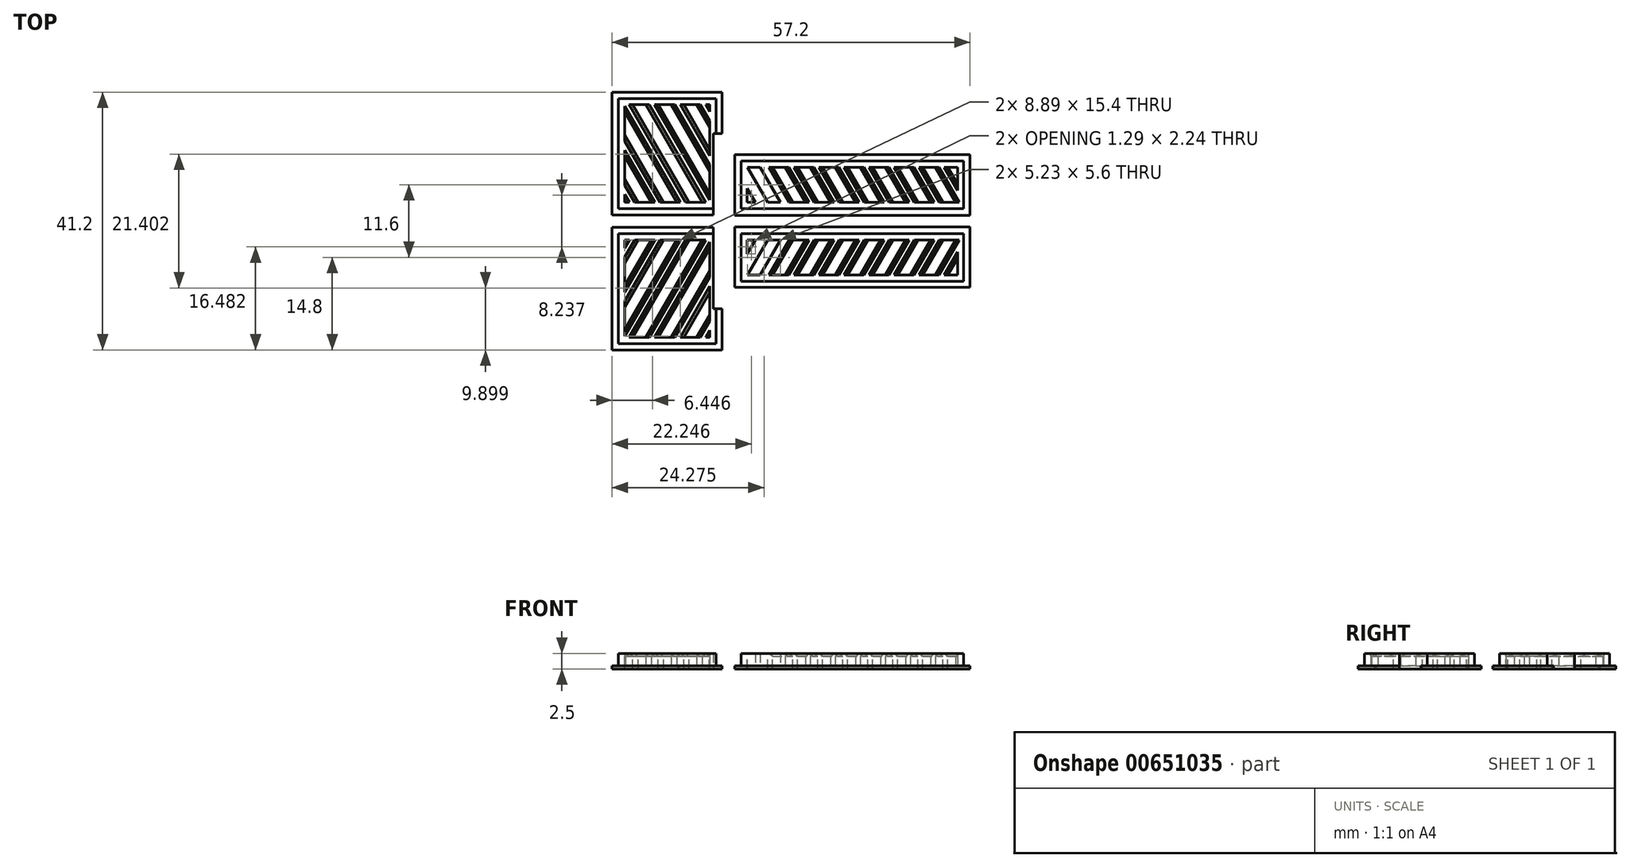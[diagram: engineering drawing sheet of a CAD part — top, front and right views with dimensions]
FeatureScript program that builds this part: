
annotation { "Feature Type Name" : "Feature", "Feature Type Description" : "" }
export const myFeature = defineFeature(function(context is Context, id is Id, definition is map)
    precondition{}
    {
        {
            var Q0;
            Q0=qCreatedBy(makeId("Top.planeOp"),FACE);
            var sketch = newSketch(context, id + "F0", { "sketchPlane" : qUnion([Q0])});
            skLineSegment(sketch, "E0.bottom", {"start": v(-17.6, 0) * mm, "end": v(-2, 0) * mm});
            skLineSegment(sketch, "E0.top", {"start": v(-17.6, 17.6) * mm, "end": v(-2, 17.6) * mm});
            skLineSegment(sketch, "E0.left", {"start": v(-17.6, 0) * mm, "end": v(-17.6, 17.6) * mm});
            skLineSegment(sketch, "E0.right", {"start": v(-2, 0) * mm, "end": v(-2, 17.6) * mm});
            skSolve(sketch);
        }
        {
            var Q0;
            Q0 = qSketchRegion(id + "F0", true);
            extrude(context, id + "F1", {"entities" : qUnion([Q0]), "depth" : 2.5 * mm, "offsetDistance" : 25 * mm});
        }
        {
            var Q0;
            Q0=qCreatedBy(makeId("Top.planeOp"),FACE);
            var sketch = newSketch(context, id + "F2", { "sketchPlane" : qUnion([Q0])});
            skLineSegment(sketch, "E1", {"start": v(-15.85, 0) * mm, "end": v(-26.01, 17.6) * mm});
            skLineSegment(sketch, "E2", {"start": v(-26.01, 17.6) * mm, "end": v(-24.01, 17.6) * mm});
            skLineSegment(sketch, "E3", {"start": v(-24.01, 17.6) * mm, "end": v(-13.85, 0) * mm});
            skLineSegment(sketch, "E4", {"start": v(-13.85, 0) * mm, "end": v(-15.85, 0) * mm});
            skLineSegment(sketch, "E5.1.0.0", {"start": v(-19.94, 17.6) * mm, "end": v(-9.78, 0) * mm});
            skLineSegment(sketch, "E5.1.0.1", {"start": v(-11.78, 0) * mm, "end": v(-21.94, 17.6) * mm});
            skLineSegment(sketch, "E5.1.0.2", {"start": v(-9.78, 0) * mm, "end": v(-11.78, 0) * mm});
            skLineSegment(sketch, "E5.1.0.3", {"start": v(-21.94, 17.6) * mm, "end": v(-19.94, 17.6) * mm});
            skLineSegment(sketch, "E5.2.0.0", {"start": v(-15.87, 17.6) * mm, "end": v(-5.7, 0) * mm});
            skLineSegment(sketch, "E5.2.0.1", {"start": v(-7.7, 0) * mm, "end": v(-17.87, 17.6) * mm});
            skLineSegment(sketch, "E5.2.0.2", {"start": v(-5.7, 0) * mm, "end": v(-7.7, 0) * mm});
            skLineSegment(sketch, "E5.2.0.3", {"start": v(-17.87, 17.6) * mm, "end": v(-15.87, 17.6) * mm});
            skLineSegment(sketch, "E5.3.0.0", {"start": v(-11.8, 17.6) * mm, "end": v(-1.64, 0) * mm});
            skLineSegment(sketch, "E5.3.0.1", {"start": v(-3.64, 0) * mm, "end": v(-13.8, 17.6) * mm});
            skLineSegment(sketch, "E5.3.0.2", {"start": v(-1.64, 0) * mm, "end": v(-3.64, 0) * mm});
            skLineSegment(sketch, "E5.3.0.3", {"start": v(-13.8, 17.6) * mm, "end": v(-11.8, 17.6) * mm});
            skLineSegment(sketch, "E5.4.0.0", {"start": v(-7.73, 17.6) * mm, "end": v(2.43, 0) * mm});
            skLineSegment(sketch, "E5.4.0.1", {"start": v(0.43, 0) * mm, "end": v(-9.73, 17.6) * mm});
            skLineSegment(sketch, "E5.4.0.2", {"start": v(2.43, 0) * mm, "end": v(0.43, 0) * mm});
            skLineSegment(sketch, "E5.4.0.3", {"start": v(-9.73, 17.6) * mm, "end": v(-7.73, 17.6) * mm});
            skLineSegment(sketch, "E5.direction1", {"start": v(-15.85, 0) * mm, "end": v(-11.78, 0) * mm, "construction": true});
            skLineSegment(sketch, "E6.0.5.0", {"start": v(-3.66, 17.6) * mm, "end": v(6.5, 0) * mm});
            skLineSegment(sketch, "E6.3.5.0", {"start": v(4.5, 0) * mm, "end": v(-5.66, 17.6) * mm});
            skLineSegment(sketch, "E6.6.5.0", {"start": v(6.5, 0) * mm, "end": v(4.5, 0) * mm});
            skLineSegment(sketch, "E6.9.5.0", {"start": v(-5.66, 17.6) * mm, "end": v(-3.66, 17.6) * mm});
            skLineSegment(sketch, "E7.bottom", {"start": v(-27.74, 19.26) * mm, "end": v(8.02, 19.26) * mm});
            skLineSegment(sketch, "E7.top", {"start": v(-27.74, -2) * mm, "end": v(8.02, -2) * mm});
            skLineSegment(sketch, "E7.left", {"start": v(-27.74, 19.26) * mm, "end": v(-27.74, -2) * mm});
            skLineSegment(sketch, "E7.right", {"start": v(8.02, 19.26) * mm, "end": v(8.02, -2) * mm});
            skSolve(sketch);
        }
        {
            var Q0;
            Q0 = qSketchRegion(id + "F2", true);
            extrude(context, id + "F3", {"entities" : qUnion([Q0]), "operationType" : NewBodyOperationType.REMOVE, "depth" : 10 * mm, "offsetDistance" : 25 * mm});
        }
        {
            var Q0;
            Q0=qCreatedBy(makeId("Top.planeOp"),FACE);
            var sketch = newSketch(context, id + "F4", { "sketchPlane" : qUnion([Q0])});
            skLineSegment(sketch, "E8.bottom", {"start": v(-17.6, 17.6) * mm, "end": v(-2, 17.6) * mm});
            skLineSegment(sketch, "E8.top", {"start": v(-17.6, 0) * mm, "end": v(-2, 0) * mm});
            skLineSegment(sketch, "E8.left", {"start": v(-17.6, 17.6) * mm, "end": v(-17.6, 0) * mm});
            skLineSegment(sketch, "E8.right", {"start": v(-2, 17.6) * mm, "end": v(-2, 0) * mm});
            skLineSegment(sketch, "E9.bottom", {"start": v(-16.6, 16.6) * mm, "end": v(-3, 16.6) * mm});
            skLineSegment(sketch, "E9.top", {"start": v(-16.6, 1) * mm, "end": v(-3, 1) * mm});
            skLineSegment(sketch, "E9.left", {"start": v(-16.6, 16.6) * mm, "end": v(-16.6, 1) * mm});
            skLineSegment(sketch, "E9.right", {"start": v(-3, 16.6) * mm, "end": v(-3, 1) * mm});
            skSolve(sketch);
        }
        {
            var Q0;
            Q0 = qSketchRegion(id + "F4", true);
            extrude(context, id + "F5", {"entities" : qUnion([Q0]), "operationType" : NewBodyOperationType.ADD, "depth" : 2.5 * mm, "offsetDistance" : 25 * mm});
        }
        {
            var Q0;
            {var subQ0=sQuery(id+"F0.wireOp",EDGE,"E0.top");var subQ2=sQuery(id+"F0.wireOp",EDGE,"E0.right");var subQ4=sQuery(id+"F0.wireOp",EDGE,"E0.bottom");var subQ6=sQuery(id+"F0.wireOp",EDGE,"E0.left");var subQ7=makeQuery(id+"F1.opExtrude","CAP_FACE",FACE,{"disambiguationData":[OSD([subQ4,subQ0,subQ6,subQ2])],"isStart":true});Q0=makeQuery(id+"F5.boolean.opBoolean","MERGE",FACE,{"derivedFrom":[makeQuery(id+"F3.boolean.opBoolean","SPLIT",FACE,{"disambiguationData":[TD([makeQuery(id+"F3.opExtrude","SWEPT_FACE",FACE,{"disambiguationData":[OSD([sQuery(id+"F2.wireOp",EDGE,"E1")])]})])],"derivedFrom":subQ7}),makeQuery(id+"F3.boolean.opBoolean","SPLIT",FACE,{"disambiguationData":[TD([makeQuery(id+"F3.opExtrude","SWEPT_FACE",FACE,{"disambiguationData":[OSD([sQuery(id+"F2.wireOp",EDGE,"E5.1.0.0")])]})])],"derivedFrom":subQ7}),makeQuery(id+"F3.boolean.opBoolean","SPLIT",FACE,{"disambiguationData":[TD([makeQuery(id+"F3.opExtrude","SWEPT_FACE",FACE,{"disambiguationData":[OSD([sQuery(id+"F2.wireOp",EDGE,"E5.4.0.0")])]})])],"derivedFrom":subQ7}),makeQuery(id+"F3.boolean.opBoolean","SPLIT",FACE,{"disambiguationData":[TD([makeQuery(id+"F3.opExtrude","SWEPT_FACE",FACE,{"disambiguationData":[OSD([sQuery(id+"F2.wireOp",EDGE,"E6.0.5.0")])]})])],"derivedFrom":subQ7}),makeQuery(id+"F3.boolean.opBoolean","SPLIT",FACE,{"disambiguationData":[TD([makeQuery(id+"F3.opExtrude","SWEPT_FACE",FACE,{"disambiguationData":[OSD([sQuery(id+"F2.wireOp",EDGE,"E5.2.0.0")])]})])],"derivedFrom":subQ7}),makeQuery(id+"F3.boolean.opBoolean","SPLIT",FACE,{"disambiguationData":[TD([makeQuery(id+"F3.opExtrude","SWEPT_FACE",FACE,{"disambiguationData":[OSD([sQuery(id+"F2.wireOp",EDGE,"E5.3.0.0")])]})])],"derivedFrom":subQ7}),makeQuery(id+"F5.opExtrude","CAP_FACE",FACE,{"disambiguationData":[OSD([sQuery(id+"F4.wireOp",EDGE,"E8.bottom"),sQuery(id+"F4.wireOp",EDGE,"E8.top"),sQuery(id+"F4.wireOp",EDGE,"E8.left"),sQuery(id+"F4.wireOp",EDGE,"E8.right"),sQuery(id+"F4.wireOp",EDGE,"E9.bottom"),sQuery(id+"F4.wireOp",EDGE,"E9.top"),sQuery(id+"F4.wireOp",EDGE,"E9.left"),sQuery(id+"F4.wireOp",EDGE,"E9.right")])],"isStart":true})]});}
            var sketch = newSketch(context, id + "F6", { "sketchPlane" : qUnion([Q0])});
            skLineSegment(sketch, "E10.bottom", {"start": v(-18.6, -18.6) * mm, "end": v(-1, -18.6) * mm});
            skLineSegment(sketch, "E10.top", {"start": v(-18.6, 1) * mm, "end": v(-1, 1) * mm});
            skLineSegment(sketch, "E10.left", {"start": v(-18.6, -18.6) * mm, "end": v(-18.6, 1) * mm});
            skLineSegment(sketch, "E10.right", {"start": v(-1, -18.6) * mm, "end": v(-1, 1) * mm});
            skLineSegment(sketch, "E11.bottom", {"start": v(-17.6, -17.6) * mm, "end": v(-2, -17.6) * mm});
            skLineSegment(sketch, "E11.top", {"start": v(-17.6, 0) * mm, "end": v(-2, 0) * mm});
            skLineSegment(sketch, "E11.left", {"start": v(-17.6, -17.6) * mm, "end": v(-17.6, 0) * mm});
            skLineSegment(sketch, "E11.right", {"start": v(-2, -17.6) * mm, "end": v(-2, 0) * mm});
            skSolve(sketch);
        }
        {
            var Q0;
            Q0 = qSketchRegion(id + "F6", true);
            extrude(context, id + "F7", {"entities" : qUnion([Q0]), "operationType" : NewBodyOperationType.ADD, "oppositeDirection" : true, "depth" : .5 * mm, "offsetDistance" : 25 * mm});
        }
        {
            var Q0;
            Q0=makeQuery(id+"F3.boolean.opBoolean","INTERSECT",EDGE,{"derivedFrom":[makeQuery(id+"F1.opExtrude","CAP_FACE",FACE,{"disambiguationData":[OSD([sQuery(id+"F0.wireOp",EDGE,"E0.bottom"),sQuery(id+"F0.wireOp",EDGE,"E0.top"),sQuery(id+"F0.wireOp",EDGE,"E0.left"),sQuery(id+"F0.wireOp",EDGE,"E0.right")])],"isStart":false}),makeQuery(id+"F3.opExtrude","SWEPT_FACE",FACE,{"disambiguationData":[OSD([sQuery(id+"F2.wireOp",EDGE,"E3")])]})]});
            var Q1;
            Q1=makeQuery(id+"F3.boolean.opBoolean","INTERSECT",EDGE,{"derivedFrom":[makeQuery(id+"F1.opExtrude","CAP_FACE",FACE,{"disambiguationData":[OSD([sQuery(id+"F0.wireOp",EDGE,"E0.bottom"),sQuery(id+"F0.wireOp",EDGE,"E0.top"),sQuery(id+"F0.wireOp",EDGE,"E0.left"),sQuery(id+"F0.wireOp",EDGE,"E0.right")])],"isStart":false}),makeQuery(id+"F3.opExtrude","SWEPT_FACE",FACE,{"disambiguationData":[OSD([sQuery(id+"F2.wireOp",EDGE,"E5.1.0.1")])]})]});
            var Q2;
            Q2=makeQuery(id+"F3.boolean.opBoolean","COPY",EDGE,{"derivedFrom":makeQuery(id+"F3.opExtrude","CAP_EDGE",EDGE,{"disambiguationData":[OSD([sQuery(id+"F2.wireOp",EDGE,"E5.2.0.1")])],"isStart":true})});
            var Q3;
            Q3=makeQuery(id+"F3.boolean.opBoolean","INTERSECT",EDGE,{"derivedFrom":[makeQuery(id+"F1.opExtrude","CAP_FACE",FACE,{"disambiguationData":[OSD([sQuery(id+"F0.wireOp",EDGE,"E0.bottom"),sQuery(id+"F0.wireOp",EDGE,"E0.top"),sQuery(id+"F0.wireOp",EDGE,"E0.left"),sQuery(id+"F0.wireOp",EDGE,"E0.right")])],"isStart":false}),makeQuery(id+"F3.opExtrude","SWEPT_FACE",FACE,{"disambiguationData":[OSD([sQuery(id+"F2.wireOp",EDGE,"E5.2.0.0")])]})]});
            var Q4;
            Q4=makeQuery(id+"F3.boolean.opBoolean","INTERSECT",EDGE,{"derivedFrom":[makeQuery(id+"F1.opExtrude","CAP_FACE",FACE,{"disambiguationData":[OSD([sQuery(id+"F0.wireOp",EDGE,"E0.bottom"),sQuery(id+"F0.wireOp",EDGE,"E0.top"),sQuery(id+"F0.wireOp",EDGE,"E0.left"),sQuery(id+"F0.wireOp",EDGE,"E0.right")])],"isStart":false}),makeQuery(id+"F3.opExtrude","SWEPT_FACE",FACE,{"disambiguationData":[OSD([sQuery(id+"F2.wireOp",EDGE,"E5.3.0.1")])]})]});
            var Q5;
            Q5=makeQuery(id+"F3.boolean.opBoolean","INTERSECT",EDGE,{"derivedFrom":[makeQuery(id+"F1.opExtrude","CAP_FACE",FACE,{"disambiguationData":[OSD([sQuery(id+"F0.wireOp",EDGE,"E0.bottom"),sQuery(id+"F0.wireOp",EDGE,"E0.top"),sQuery(id+"F0.wireOp",EDGE,"E0.left"),sQuery(id+"F0.wireOp",EDGE,"E0.right")])],"isStart":false}),makeQuery(id+"F3.opExtrude","SWEPT_FACE",FACE,{"disambiguationData":[OSD([sQuery(id+"F2.wireOp",EDGE,"E5.3.0.0")])]})]});
            var Q6;
            Q6=makeQuery(id+"F3.boolean.opBoolean","INTERSECT",EDGE,{"derivedFrom":[makeQuery(id+"F1.opExtrude","CAP_FACE",FACE,{"disambiguationData":[OSD([sQuery(id+"F0.wireOp",EDGE,"E0.bottom"),sQuery(id+"F0.wireOp",EDGE,"E0.top"),sQuery(id+"F0.wireOp",EDGE,"E0.left"),sQuery(id+"F0.wireOp",EDGE,"E0.right")])],"isStart":false}),makeQuery(id+"F3.opExtrude","SWEPT_FACE",FACE,{"disambiguationData":[OSD([sQuery(id+"F2.wireOp",EDGE,"E5.4.0.1")])]})]});
            var Q7;
            Q7=makeQuery(id+"F3.boolean.opBoolean","INTERSECT",EDGE,{"derivedFrom":[makeQuery(id+"F1.opExtrude","CAP_FACE",FACE,{"disambiguationData":[OSD([sQuery(id+"F0.wireOp",EDGE,"E0.bottom"),sQuery(id+"F0.wireOp",EDGE,"E0.top"),sQuery(id+"F0.wireOp",EDGE,"E0.left"),sQuery(id+"F0.wireOp",EDGE,"E0.right")])],"isStart":false}),makeQuery(id+"F3.opExtrude","SWEPT_FACE",FACE,{"disambiguationData":[OSD([sQuery(id+"F2.wireOp",EDGE,"E5.4.0.0")])]})]});
            var Q8;
            Q8=makeQuery(id+"F3.boolean.opBoolean","INTERSECT",EDGE,{"derivedFrom":[makeQuery(id+"F1.opExtrude","CAP_FACE",FACE,{"disambiguationData":[OSD([sQuery(id+"F0.wireOp",EDGE,"E0.bottom"),sQuery(id+"F0.wireOp",EDGE,"E0.top"),sQuery(id+"F0.wireOp",EDGE,"E0.left"),sQuery(id+"F0.wireOp",EDGE,"E0.right")])],"isStart":false}),makeQuery(id+"F3.opExtrude","SWEPT_FACE",FACE,{"disambiguationData":[OSD([sQuery(id+"F2.wireOp",EDGE,"E6.3.5.0")])]})]});
            var Q9;
            Q9=makeQuery(id+"F3.boolean.opBoolean","INTERSECT",EDGE,{"derivedFrom":[makeQuery(id+"F1.opExtrude","CAP_FACE",FACE,{"disambiguationData":[OSD([sQuery(id+"F0.wireOp",EDGE,"E0.bottom"),sQuery(id+"F0.wireOp",EDGE,"E0.top"),sQuery(id+"F0.wireOp",EDGE,"E0.left"),sQuery(id+"F0.wireOp",EDGE,"E0.right")])],"isStart":false}),makeQuery(id+"F3.opExtrude","SWEPT_FACE",FACE,{"disambiguationData":[OSD([sQuery(id+"F2.wireOp",EDGE,"E1")])]})]});
            var Q10;
            Q10=makeQuery(id+"F3.boolean.opBoolean","INTERSECT",EDGE,{"derivedFrom":[makeQuery(id+"F1.opExtrude","CAP_FACE",FACE,{"disambiguationData":[OSD([sQuery(id+"F0.wireOp",EDGE,"E0.bottom"),sQuery(id+"F0.wireOp",EDGE,"E0.top"),sQuery(id+"F0.wireOp",EDGE,"E0.left"),sQuery(id+"F0.wireOp",EDGE,"E0.right")])],"isStart":false}),makeQuery(id+"F3.opExtrude","SWEPT_FACE",FACE,{"disambiguationData":[OSD([sQuery(id+"F2.wireOp",EDGE,"E6.0.5.0")])]})]});
            var Q11;
            Q11=makeQuery(id+"F3.boolean.opBoolean","INTERSECT",EDGE,{"derivedFrom":[makeQuery(id+"F1.opExtrude","CAP_FACE",FACE,{"disambiguationData":[OSD([sQuery(id+"F0.wireOp",EDGE,"E0.bottom"),sQuery(id+"F0.wireOp",EDGE,"E0.top"),sQuery(id+"F0.wireOp",EDGE,"E0.left"),sQuery(id+"F0.wireOp",EDGE,"E0.right")])],"isStart":false}),makeQuery(id+"F3.opExtrude","SWEPT_FACE",FACE,{"disambiguationData":[OSD([sQuery(id+"F2.wireOp",EDGE,"E5.2.0.1")])]})]});
            var Q12;
            Q12=makeQuery(id+"F3.boolean.opBoolean","INTERSECT",EDGE,{"derivedFrom":[makeQuery(id+"F1.opExtrude","CAP_FACE",FACE,{"disambiguationData":[OSD([sQuery(id+"F0.wireOp",EDGE,"E0.bottom"),sQuery(id+"F0.wireOp",EDGE,"E0.top"),sQuery(id+"F0.wireOp",EDGE,"E0.left"),sQuery(id+"F0.wireOp",EDGE,"E0.right")])],"isStart":false}),makeQuery(id+"F3.opExtrude","SWEPT_FACE",FACE,{"disambiguationData":[OSD([sQuery(id+"F2.wireOp",EDGE,"E5.1.0.0")])]})]});
            chamfer(context, id + "F8", {"entities" : qUnion([Q0, Q1, Q2, Q3, Q4, Q5, Q6, Q7, Q8, Q9, Q10, Q11, Q12]), "width" : .5 * mm, "tangentPropagation" : true});
        }
        {
            var Q0;
            Q0=qCreatedBy(makeId("Top.planeOp"),FACE);
            var sketch = newSketch(context, id + "F9", { "sketchPlane" : qUnion([Q0])});
            skLineSegment(sketch, "E12.bottom", {"start": v(2, 7.6) * mm, "end": v(37.6, 7.6) * mm});
            skLineSegment(sketch, "E12.top", {"start": v(2, 0) * mm, "end": v(37.6, 0) * mm});
            skLineSegment(sketch, "E12.left", {"start": v(2, 7.6) * mm, "end": v(2, 0) * mm});
            skLineSegment(sketch, "E12.right", {"start": v(37.6, 7.6) * mm, "end": v(37.6, 0) * mm});
            skSolve(sketch);
        }
        {
            var Q0;
            Q0 = qSketchRegion(id + "F9", true);
            extrude(context, id + "F10", {"entities" : qUnion([Q0]), "depth" : 2.5 * mm, "offsetDistance" : 25 * mm});
        }
        {
            var Q0;
            Q0=qCreatedBy(makeId("Top.planeOp"),FACE);
            var sketch = newSketch(context, id + "F11", { "sketchPlane" : qUnion([Q0])});
            skLineSegment(sketch, "E13", {"start": v(4.87, 0) * mm, "end": v(0.25, 8) * mm});
            skLineSegment(sketch, "E14", {"start": v(0.25, 8) * mm, "end": v(2.25, 8) * mm});
            skLineSegment(sketch, "E15", {"start": v(2.25, 8) * mm, "end": v(6.87, 0) * mm});
            skLineSegment(sketch, "E16", {"start": v(6.87, 0) * mm, "end": v(4.87, 0) * mm});
            skLineSegment(sketch, "E17.1.0.0", {"start": v(10.87, 0) * mm, "end": v(8.87, 0) * mm});
            skLineSegment(sketch, "E17.1.0.1", {"start": v(6.25, 8) * mm, "end": v(10.87, 0) * mm});
            skLineSegment(sketch, "E17.1.0.2", {"start": v(8.87, 0) * mm, "end": v(4.25, 8) * mm});
            skLineSegment(sketch, "E17.1.0.3", {"start": v(4.25, 8) * mm, "end": v(6.25, 8) * mm});
            skLineSegment(sketch, "E17.2.0.0", {"start": v(14.87, 0) * mm, "end": v(12.87, 0) * mm});
            skLineSegment(sketch, "E17.2.0.1", {"start": v(10.25, 8) * mm, "end": v(14.87, 0) * mm});
            skLineSegment(sketch, "E17.2.0.2", {"start": v(12.87, 0) * mm, "end": v(8.25, 8) * mm});
            skLineSegment(sketch, "E17.2.0.3", {"start": v(8.25, 8) * mm, "end": v(10.25, 8) * mm});
            skLineSegment(sketch, "E17.3.0.0", {"start": v(18.87, 0) * mm, "end": v(16.87, 0) * mm});
            skLineSegment(sketch, "E17.3.0.1", {"start": v(14.25, 8) * mm, "end": v(18.87, 0) * mm});
            skLineSegment(sketch, "E17.3.0.2", {"start": v(16.87, 0) * mm, "end": v(12.25, 8) * mm});
            skLineSegment(sketch, "E17.3.0.3", {"start": v(12.25, 8) * mm, "end": v(14.25, 8) * mm});
            skLineSegment(sketch, "E17.4.0.0", {"start": v(22.87, 0) * mm, "end": v(20.87, 0) * mm});
            skLineSegment(sketch, "E17.4.0.1", {"start": v(18.25, 8) * mm, "end": v(22.87, 0) * mm});
            skLineSegment(sketch, "E17.4.0.2", {"start": v(20.87, 0) * mm, "end": v(16.25, 8) * mm});
            skLineSegment(sketch, "E17.4.0.3", {"start": v(16.25, 8) * mm, "end": v(18.25, 8) * mm});
            skLineSegment(sketch, "E17.5.0.0", {"start": v(26.87, 0) * mm, "end": v(24.87, 0) * mm});
            skLineSegment(sketch, "E17.5.0.1", {"start": v(22.25, 8) * mm, "end": v(26.87, 0) * mm});
            skLineSegment(sketch, "E17.5.0.2", {"start": v(24.87, 0) * mm, "end": v(20.25, 8) * mm});
            skLineSegment(sketch, "E17.5.0.3", {"start": v(20.25, 8) * mm, "end": v(22.25, 8) * mm});
            skLineSegment(sketch, "E17.6.0.0", {"start": v(30.87, 0) * mm, "end": v(28.87, 0) * mm});
            skLineSegment(sketch, "E17.6.0.1", {"start": v(26.25, 8) * mm, "end": v(30.87, 0) * mm});
            skLineSegment(sketch, "E17.6.0.2", {"start": v(28.87, 0) * mm, "end": v(24.25, 8) * mm});
            skLineSegment(sketch, "E17.6.0.3", {"start": v(24.25, 8) * mm, "end": v(26.25, 8) * mm});
            skLineSegment(sketch, "E17.7.0.0", {"start": v(34.87, 0) * mm, "end": v(32.87, 0) * mm});
            skLineSegment(sketch, "E17.7.0.1", {"start": v(30.25, 8) * mm, "end": v(34.87, 0) * mm});
            skLineSegment(sketch, "E17.7.0.2", {"start": v(32.87, 0) * mm, "end": v(28.25, 8) * mm});
            skLineSegment(sketch, "E17.7.0.3", {"start": v(28.25, 8) * mm, "end": v(30.25, 8) * mm});
            skLineSegment(sketch, "E17.8.0.0", {"start": v(38.87, 0) * mm, "end": v(36.87, 0) * mm});
            skLineSegment(sketch, "E17.8.0.1", {"start": v(34.25, 8) * mm, "end": v(38.87, 0) * mm});
            skLineSegment(sketch, "E17.8.0.2", {"start": v(36.87, 0) * mm, "end": v(32.25, 8) * mm});
            skLineSegment(sketch, "E17.8.0.3", {"start": v(32.25, 8) * mm, "end": v(34.25, 8) * mm});
            skLineSegment(sketch, "E17.9.0.0", {"start": v(42.87, 0) * mm, "end": v(40.87, 0) * mm});
            skLineSegment(sketch, "E17.9.0.1", {"start": v(38.25, 8) * mm, "end": v(42.87, 0) * mm});
            skLineSegment(sketch, "E17.9.0.2", {"start": v(40.87, 0) * mm, "end": v(36.25, 8) * mm});
            skLineSegment(sketch, "E17.9.0.3", {"start": v(36.25, 8) * mm, "end": v(38.25, 8) * mm});
            skLineSegment(sketch, "E17.10.0.0", {"start": v(46.87, 0) * mm, "end": v(44.87, 0) * mm});
            skLineSegment(sketch, "E17.10.0.1", {"start": v(42.25, 8) * mm, "end": v(46.87, 0) * mm});
            skLineSegment(sketch, "E17.10.0.2", {"start": v(44.87, 0) * mm, "end": v(40.25, 8) * mm});
            skLineSegment(sketch, "E17.10.0.3", {"start": v(40.25, 8) * mm, "end": v(42.25, 8) * mm});
            skLineSegment(sketch, "E17.11.0.0", {"start": v(50.87, 0) * mm, "end": v(48.87, 0) * mm});
            skLineSegment(sketch, "E17.11.0.1", {"start": v(46.25, 8) * mm, "end": v(50.87, 0) * mm});
            skLineSegment(sketch, "E17.11.0.2", {"start": v(48.87, 0) * mm, "end": v(44.25, 8) * mm});
            skLineSegment(sketch, "E17.11.0.3", {"start": v(44.25, 8) * mm, "end": v(46.25, 8) * mm});
            skLineSegment(sketch, "E17.12.0.0", {"start": v(54.87, 0) * mm, "end": v(52.87, 0) * mm});
            skLineSegment(sketch, "E17.12.0.1", {"start": v(50.25, 8) * mm, "end": v(54.87, 0) * mm});
            skLineSegment(sketch, "E17.12.0.2", {"start": v(52.87, 0) * mm, "end": v(48.25, 8) * mm});
            skLineSegment(sketch, "E17.12.0.3", {"start": v(48.25, 8) * mm, "end": v(50.25, 8) * mm});
            skLineSegment(sketch, "E17.13.0.0", {"start": v(58.87, 0) * mm, "end": v(56.87, 0) * mm});
            skLineSegment(sketch, "E17.13.0.1", {"start": v(54.25, 8) * mm, "end": v(58.87, 0) * mm});
            skLineSegment(sketch, "E17.13.0.2", {"start": v(56.87, 0) * mm, "end": v(52.25, 8) * mm});
            skLineSegment(sketch, "E17.13.0.3", {"start": v(52.25, 8) * mm, "end": v(54.25, 8) * mm});
            skLineSegment(sketch, "E17.14.0.0", {"start": v(62.87, 0) * mm, "end": v(60.87, 0) * mm});
            skLineSegment(sketch, "E17.14.0.1", {"start": v(58.25, 8) * mm, "end": v(62.87, 0) * mm});
            skLineSegment(sketch, "E17.14.0.2", {"start": v(60.87, 0) * mm, "end": v(56.25, 8) * mm});
            skLineSegment(sketch, "E17.14.0.3", {"start": v(56.25, 8) * mm, "end": v(58.25, 8) * mm});
            skLineSegment(sketch, "E17.direction1", {"start": v(4.87, 0) * mm, "end": v(8.87, 0) * mm, "construction": true});
            skLineSegment(sketch, "E18.bottom", {"start": v(-2.42, 12) * mm, "end": v(67.7, 12) * mm});
            skLineSegment(sketch, "E18.top", {"start": v(-2.42, -4) * mm, "end": v(67.7, -4) * mm});
            skLineSegment(sketch, "E18.left", {"start": v(-2.42, 12) * mm, "end": v(-2.42, -4) * mm});
            skLineSegment(sketch, "E18.right", {"start": v(67.7, 12) * mm, "end": v(67.7, -4) * mm});
            skSolve(sketch);
        }
        {
            var Q0;
            Q0 = qSketchRegion(id + "F11", true);
            extrude(context, id + "F12", {"entities" : qUnion([Q0]), "operationType" : NewBodyOperationType.REMOVE, "depth" : 25 * mm, "offsetDistance" : 25 * mm});
        }
        {
            var Q0;
            Q0=qCreatedBy(makeId("Top.planeOp"),FACE);
            var sketch = newSketch(context, id + "F13", { "sketchPlane" : qUnion([Q0])});
            skLineSegment(sketch, "E19.bottom", {"start": v(2, 7.6) * mm, "end": v(37.6, 7.6) * mm});
            skLineSegment(sketch, "E19.top", {"start": v(2, 0) * mm, "end": v(37.6, 0) * mm});
            skLineSegment(sketch, "E19.left", {"start": v(2, 7.6) * mm, "end": v(2, 0) * mm});
            skLineSegment(sketch, "E19.right", {"start": v(37.6, 7.6) * mm, "end": v(37.6, 0) * mm});
            skLineSegment(sketch, "E20.bottom", {"start": v(3, 6.6) * mm, "end": v(36.6, 6.6) * mm});
            skLineSegment(sketch, "E20.top", {"start": v(3, 1) * mm, "end": v(36.6, 1) * mm});
            skLineSegment(sketch, "E20.left", {"start": v(3, 6.6) * mm, "end": v(3, 1) * mm});
            skLineSegment(sketch, "E20.right", {"start": v(36.6, 6.6) * mm, "end": v(36.6, 1) * mm});
            skSolve(sketch);
        }
        {
            var Q0;
            Q0 = qSketchRegion(id + "F13", true);
            extrude(context, id + "F14", {"entities" : qUnion([Q0]), "operationType" : NewBodyOperationType.ADD, "depth" : 2.5 * mm, "offsetDistance" : 25 * mm});
        }
        {
            var Q0;
            {var subQ0=sQuery(id+"F9.wireOp",EDGE,"E12.bottom");var subQ2=sQuery(id+"F9.wireOp",EDGE,"E12.top");var subQ4=sQuery(id+"F9.wireOp",EDGE,"E12.right");var subQ5=sQuery(id+"F9.wireOp",EDGE,"E12.left");var subQ6=makeQuery(id+"F10.opExtrude","CAP_FACE",FACE,{"disambiguationData":[OSD([subQ0,subQ2,subQ5,subQ4])],"isStart":true});Q0=makeQuery(id+"F14.boolean.opBoolean","MERGE",FACE,{"derivedFrom":[makeQuery(id+"F12.boolean.opBoolean","SPLIT",FACE,{"disambiguationData":[TD([makeQuery(id+"F10.opExtrude","SWEPT_FACE",FACE,{"disambiguationData":[OSD([subQ5])]})])],"derivedFrom":subQ6}),makeQuery(id+"F12.boolean.opBoolean","SPLIT",FACE,{"disambiguationData":[TD([makeQuery(id+"F10.opExtrude","SWEPT_FACE",FACE,{"disambiguationData":[OSD([subQ4])]})])],"derivedFrom":subQ6}),makeQuery(id+"F12.boolean.opBoolean","SPLIT",FACE,{"disambiguationData":[TD([makeQuery(id+"F12.opExtrude","SWEPT_FACE",FACE,{"disambiguationData":[OSD([sQuery(id+"F11.wireOp",EDGE,"E17.2.0.1")])]})])],"derivedFrom":subQ6}),makeQuery(id+"F12.boolean.opBoolean","SPLIT",FACE,{"disambiguationData":[TD([makeQuery(id+"F12.opExtrude","SWEPT_FACE",FACE,{"disambiguationData":[OSD([sQuery(id+"F11.wireOp",EDGE,"E17.3.0.1")])]})])],"derivedFrom":subQ6}),makeQuery(id+"F12.boolean.opBoolean","SPLIT",FACE,{"disambiguationData":[TD([makeQuery(id+"F12.opExtrude","SWEPT_FACE",FACE,{"disambiguationData":[OSD([sQuery(id+"F11.wireOp",EDGE,"E17.4.0.1")])]})])],"derivedFrom":subQ6}),makeQuery(id+"F12.boolean.opBoolean","SPLIT",FACE,{"disambiguationData":[TD([makeQuery(id+"F12.opExtrude","SWEPT_FACE",FACE,{"disambiguationData":[OSD([sQuery(id+"F11.wireOp",EDGE,"E17.5.0.1")])]})])],"derivedFrom":subQ6}),makeQuery(id+"F12.boolean.opBoolean","SPLIT",FACE,{"disambiguationData":[TD([makeQuery(id+"F12.opExtrude","SWEPT_FACE",FACE,{"disambiguationData":[OSD([sQuery(id+"F11.wireOp",EDGE,"E17.6.0.1")])]})])],"derivedFrom":subQ6}),makeQuery(id+"F12.boolean.opBoolean","SPLIT",FACE,{"disambiguationData":[TD([makeQuery(id+"F12.opExtrude","SWEPT_FACE",FACE,{"disambiguationData":[OSD([sQuery(id+"F11.wireOp",EDGE,"E17.7.0.1")])]})])],"derivedFrom":subQ6}),makeQuery(id+"F12.boolean.opBoolean","SPLIT",FACE,{"disambiguationData":[TD([makeQuery(id+"F12.opExtrude","SWEPT_FACE",FACE,{"disambiguationData":[OSD([sQuery(id+"F11.wireOp",EDGE,"E17.8.0.1")])]})])],"derivedFrom":subQ6}),makeQuery(id+"F12.boolean.opBoolean","SPLIT",FACE,{"disambiguationData":[TD([makeQuery(id+"F12.opExtrude","SWEPT_FACE",FACE,{"disambiguationData":[OSD([sQuery(id+"F11.wireOp",EDGE,"E17.9.0.1")])]})])],"derivedFrom":subQ6}),makeQuery(id+"F14.opExtrude","CAP_FACE",FACE,{"disambiguationData":[OSD([sQuery(id+"F13.wireOp",EDGE,"E19.bottom"),sQuery(id+"F13.wireOp",EDGE,"E19.top"),sQuery(id+"F13.wireOp",EDGE,"E19.left"),sQuery(id+"F13.wireOp",EDGE,"E19.right"),sQuery(id+"F13.wireOp",EDGE,"E20.bottom"),sQuery(id+"F13.wireOp",EDGE,"E20.top"),sQuery(id+"F13.wireOp",EDGE,"E20.left"),sQuery(id+"F13.wireOp",EDGE,"E20.right")])],"isStart":true})]});}
            var sketch = newSketch(context, id + "F15", { "sketchPlane" : qUnion([Q0])});
            skLineSegment(sketch, "E21.bottom", {"start": v(1, -8.6) * mm, "end": v(38.6, -8.6) * mm});
            skLineSegment(sketch, "E21.top", {"start": v(1, 1.09) * mm, "end": v(38.6, 1.09) * mm});
            skLineSegment(sketch, "E21.left", {"start": v(1, -8.6) * mm, "end": v(1, 1.09) * mm});
            skLineSegment(sketch, "E21.right", {"start": v(38.6, -8.6) * mm, "end": v(38.6, 1.09) * mm});
            skLineSegment(sketch, "E22.bottom", {"start": v(2, -7.6) * mm, "end": v(37.6, -7.6) * mm});
            skLineSegment(sketch, "E22.top", {"start": v(2, 0) * mm, "end": v(37.6, 0) * mm});
            skLineSegment(sketch, "E22.left", {"start": v(2, -7.6) * mm, "end": v(2, 0) * mm});
            skLineSegment(sketch, "E22.right", {"start": v(37.6, -7.6) * mm, "end": v(37.6, 0) * mm});
            skSolve(sketch);
        }
        {
            var Q0;
            Q0 = qSketchRegion(id + "F15", true);
            extrude(context, id + "F16", {"entities" : qUnion([Q0]), "operationType" : NewBodyOperationType.ADD, "oppositeDirection" : true, "depth" : .5 * mm, "offsetDistance" : 25 * mm});
        }
        {
            var Q0;
            Q0=makeQuery(id+"F12.boolean.opBoolean","INTERSECT",EDGE,{"derivedFrom":[makeQuery(id+"F10.opExtrude","CAP_FACE",FACE,{"disambiguationData":[OSD([sQuery(id+"F9.wireOp",EDGE,"E12.bottom"),sQuery(id+"F9.wireOp",EDGE,"E12.top"),sQuery(id+"F9.wireOp",EDGE,"E12.left"),sQuery(id+"F9.wireOp",EDGE,"E12.right")])],"isStart":false}),makeQuery(id+"F12.opExtrude","SWEPT_FACE",FACE,{"disambiguationData":[OSD([sQuery(id+"F11.wireOp",EDGE,"E17.1.0.1")])]})]});
            var Q1;
            Q1=makeQuery(id+"F12.boolean.opBoolean","INTERSECT",EDGE,{"derivedFrom":[makeQuery(id+"F10.opExtrude","CAP_FACE",FACE,{"disambiguationData":[OSD([sQuery(id+"F9.wireOp",EDGE,"E12.bottom"),sQuery(id+"F9.wireOp",EDGE,"E12.top"),sQuery(id+"F9.wireOp",EDGE,"E12.left"),sQuery(id+"F9.wireOp",EDGE,"E12.right")])],"isStart":false}),makeQuery(id+"F12.opExtrude","SWEPT_FACE",FACE,{"disambiguationData":[OSD([sQuery(id+"F11.wireOp",EDGE,"E17.2.0.2")])]})]});
            var Q2;
            Q2=makeQuery(id+"F12.boolean.opBoolean","INTERSECT",EDGE,{"derivedFrom":[makeQuery(id+"F10.opExtrude","CAP_FACE",FACE,{"disambiguationData":[OSD([sQuery(id+"F9.wireOp",EDGE,"E12.bottom"),sQuery(id+"F9.wireOp",EDGE,"E12.top"),sQuery(id+"F9.wireOp",EDGE,"E12.left"),sQuery(id+"F9.wireOp",EDGE,"E12.right")])],"isStart":false}),makeQuery(id+"F12.opExtrude","SWEPT_FACE",FACE,{"disambiguationData":[OSD([sQuery(id+"F11.wireOp",EDGE,"E17.2.0.1")])]})]});
            var Q3;
            Q3=makeQuery(id+"F12.boolean.opBoolean","INTERSECT",EDGE,{"derivedFrom":[makeQuery(id+"F10.opExtrude","CAP_FACE",FACE,{"disambiguationData":[OSD([sQuery(id+"F9.wireOp",EDGE,"E12.bottom"),sQuery(id+"F9.wireOp",EDGE,"E12.top"),sQuery(id+"F9.wireOp",EDGE,"E12.left"),sQuery(id+"F9.wireOp",EDGE,"E12.right")])],"isStart":false}),makeQuery(id+"F12.opExtrude","SWEPT_FACE",FACE,{"disambiguationData":[OSD([sQuery(id+"F11.wireOp",EDGE,"E17.3.0.2")])]})]});
            var Q4;
            Q4=makeQuery(id+"F12.boolean.opBoolean","INTERSECT",EDGE,{"derivedFrom":[makeQuery(id+"F10.opExtrude","CAP_FACE",FACE,{"disambiguationData":[OSD([sQuery(id+"F9.wireOp",EDGE,"E12.bottom"),sQuery(id+"F9.wireOp",EDGE,"E12.top"),sQuery(id+"F9.wireOp",EDGE,"E12.left"),sQuery(id+"F9.wireOp",EDGE,"E12.right")])],"isStart":false}),makeQuery(id+"F12.opExtrude","SWEPT_FACE",FACE,{"disambiguationData":[OSD([sQuery(id+"F11.wireOp",EDGE,"E17.3.0.1")])]})]});
            var Q5;
            Q5=makeQuery(id+"F12.boolean.opBoolean","INTERSECT",EDGE,{"derivedFrom":[makeQuery(id+"F10.opExtrude","CAP_FACE",FACE,{"disambiguationData":[OSD([sQuery(id+"F9.wireOp",EDGE,"E12.bottom"),sQuery(id+"F9.wireOp",EDGE,"E12.top"),sQuery(id+"F9.wireOp",EDGE,"E12.left"),sQuery(id+"F9.wireOp",EDGE,"E12.right")])],"isStart":false}),makeQuery(id+"F12.opExtrude","SWEPT_FACE",FACE,{"disambiguationData":[OSD([sQuery(id+"F11.wireOp",EDGE,"E17.4.0.2")])]})]});
            var Q6;
            Q6=makeQuery(id+"F12.boolean.opBoolean","INTERSECT",EDGE,{"derivedFrom":[makeQuery(id+"F10.opExtrude","CAP_FACE",FACE,{"disambiguationData":[OSD([sQuery(id+"F9.wireOp",EDGE,"E12.bottom"),sQuery(id+"F9.wireOp",EDGE,"E12.top"),sQuery(id+"F9.wireOp",EDGE,"E12.left"),sQuery(id+"F9.wireOp",EDGE,"E12.right")])],"isStart":false}),makeQuery(id+"F12.opExtrude","SWEPT_FACE",FACE,{"disambiguationData":[OSD([sQuery(id+"F11.wireOp",EDGE,"E17.4.0.1")])]})]});
            var Q7;
            Q7=makeQuery(id+"F12.boolean.opBoolean","INTERSECT",EDGE,{"derivedFrom":[makeQuery(id+"F10.opExtrude","CAP_FACE",FACE,{"disambiguationData":[OSD([sQuery(id+"F9.wireOp",EDGE,"E12.bottom"),sQuery(id+"F9.wireOp",EDGE,"E12.top"),sQuery(id+"F9.wireOp",EDGE,"E12.left"),sQuery(id+"F9.wireOp",EDGE,"E12.right")])],"isStart":false}),makeQuery(id+"F12.opExtrude","SWEPT_FACE",FACE,{"disambiguationData":[OSD([sQuery(id+"F11.wireOp",EDGE,"E17.5.0.2")])]})]});
            var Q8;
            Q8=makeQuery(id+"F12.boolean.opBoolean","INTERSECT",EDGE,{"derivedFrom":[makeQuery(id+"F10.opExtrude","CAP_FACE",FACE,{"disambiguationData":[OSD([sQuery(id+"F9.wireOp",EDGE,"E12.bottom"),sQuery(id+"F9.wireOp",EDGE,"E12.top"),sQuery(id+"F9.wireOp",EDGE,"E12.left"),sQuery(id+"F9.wireOp",EDGE,"E12.right")])],"isStart":false}),makeQuery(id+"F12.opExtrude","SWEPT_FACE",FACE,{"disambiguationData":[OSD([sQuery(id+"F11.wireOp",EDGE,"E17.5.0.1")])]})]});
            var Q9;
            Q9=makeQuery(id+"F12.boolean.opBoolean","INTERSECT",EDGE,{"derivedFrom":[makeQuery(id+"F10.opExtrude","CAP_FACE",FACE,{"disambiguationData":[OSD([sQuery(id+"F9.wireOp",EDGE,"E12.bottom"),sQuery(id+"F9.wireOp",EDGE,"E12.top"),sQuery(id+"F9.wireOp",EDGE,"E12.left"),sQuery(id+"F9.wireOp",EDGE,"E12.right")])],"isStart":false}),makeQuery(id+"F12.opExtrude","SWEPT_FACE",FACE,{"disambiguationData":[OSD([sQuery(id+"F11.wireOp",EDGE,"E17.6.0.2")])]})]});
            var Q10;
            Q10=makeQuery(id+"F12.boolean.opBoolean","INTERSECT",EDGE,{"derivedFrom":[makeQuery(id+"F10.opExtrude","CAP_FACE",FACE,{"disambiguationData":[OSD([sQuery(id+"F9.wireOp",EDGE,"E12.bottom"),sQuery(id+"F9.wireOp",EDGE,"E12.top"),sQuery(id+"F9.wireOp",EDGE,"E12.left"),sQuery(id+"F9.wireOp",EDGE,"E12.right")])],"isStart":false}),makeQuery(id+"F12.opExtrude","SWEPT_FACE",FACE,{"disambiguationData":[OSD([sQuery(id+"F11.wireOp",EDGE,"E17.6.0.1")])]})]});
            var Q11;
            Q11=makeQuery(id+"F12.boolean.opBoolean","INTERSECT",EDGE,{"derivedFrom":[makeQuery(id+"F10.opExtrude","CAP_FACE",FACE,{"disambiguationData":[OSD([sQuery(id+"F9.wireOp",EDGE,"E12.bottom"),sQuery(id+"F9.wireOp",EDGE,"E12.top"),sQuery(id+"F9.wireOp",EDGE,"E12.left"),sQuery(id+"F9.wireOp",EDGE,"E12.right")])],"isStart":false}),makeQuery(id+"F12.opExtrude","SWEPT_FACE",FACE,{"disambiguationData":[OSD([sQuery(id+"F11.wireOp",EDGE,"E17.7.0.2")])]})]});
            var Q12;
            Q12=makeQuery(id+"F12.boolean.opBoolean","INTERSECT",EDGE,{"derivedFrom":[makeQuery(id+"F10.opExtrude","CAP_FACE",FACE,{"disambiguationData":[OSD([sQuery(id+"F9.wireOp",EDGE,"E12.bottom"),sQuery(id+"F9.wireOp",EDGE,"E12.top"),sQuery(id+"F9.wireOp",EDGE,"E12.left"),sQuery(id+"F9.wireOp",EDGE,"E12.right")])],"isStart":false}),makeQuery(id+"F12.opExtrude","SWEPT_FACE",FACE,{"disambiguationData":[OSD([sQuery(id+"F11.wireOp",EDGE,"E17.7.0.1")])]})]});
            var Q13;
            Q13=makeQuery(id+"F12.boolean.opBoolean","INTERSECT",EDGE,{"derivedFrom":[makeQuery(id+"F10.opExtrude","CAP_FACE",FACE,{"disambiguationData":[OSD([sQuery(id+"F9.wireOp",EDGE,"E12.bottom"),sQuery(id+"F9.wireOp",EDGE,"E12.top"),sQuery(id+"F9.wireOp",EDGE,"E12.left"),sQuery(id+"F9.wireOp",EDGE,"E12.right")])],"isStart":false}),makeQuery(id+"F12.opExtrude","SWEPT_FACE",FACE,{"disambiguationData":[OSD([sQuery(id+"F11.wireOp",EDGE,"E17.8.0.2")])]})]});
            var Q14;
            Q14=makeQuery(id+"F12.boolean.opBoolean","INTERSECT",EDGE,{"derivedFrom":[makeQuery(id+"F10.opExtrude","CAP_FACE",FACE,{"disambiguationData":[OSD([sQuery(id+"F9.wireOp",EDGE,"E12.bottom"),sQuery(id+"F9.wireOp",EDGE,"E12.top"),sQuery(id+"F9.wireOp",EDGE,"E12.left"),sQuery(id+"F9.wireOp",EDGE,"E12.right")])],"isStart":false}),makeQuery(id+"F12.opExtrude","SWEPT_FACE",FACE,{"disambiguationData":[OSD([sQuery(id+"F11.wireOp",EDGE,"E17.8.0.1")])]})]});
            var Q15;
            Q15=makeQuery(id+"F12.boolean.opBoolean","INTERSECT",EDGE,{"derivedFrom":[makeQuery(id+"F10.opExtrude","CAP_FACE",FACE,{"disambiguationData":[OSD([sQuery(id+"F9.wireOp",EDGE,"E12.bottom"),sQuery(id+"F9.wireOp",EDGE,"E12.top"),sQuery(id+"F9.wireOp",EDGE,"E12.left"),sQuery(id+"F9.wireOp",EDGE,"E12.right")])],"isStart":false}),makeQuery(id+"F12.opExtrude","SWEPT_FACE",FACE,{"disambiguationData":[OSD([sQuery(id+"F11.wireOp",EDGE,"E17.9.0.2")])]})]});
            var Q16;
            Q16=makeQuery(id+"F12.boolean.opBoolean","INTERSECT",EDGE,{"derivedFrom":[makeQuery(id+"F10.opExtrude","CAP_FACE",FACE,{"disambiguationData":[OSD([sQuery(id+"F9.wireOp",EDGE,"E12.bottom"),sQuery(id+"F9.wireOp",EDGE,"E12.top"),sQuery(id+"F9.wireOp",EDGE,"E12.left"),sQuery(id+"F9.wireOp",EDGE,"E12.right")])],"isStart":false}),makeQuery(id+"F12.opExtrude","SWEPT_FACE",FACE,{"disambiguationData":[OSD([sQuery(id+"F11.wireOp",EDGE,"E17.9.0.1")])]})]});
            var Q17;
            Q17=makeQuery(id+"F12.boolean.opBoolean","INTERSECT",EDGE,{"derivedFrom":[makeQuery(id+"F10.opExtrude","CAP_FACE",FACE,{"disambiguationData":[OSD([sQuery(id+"F9.wireOp",EDGE,"E12.bottom"),sQuery(id+"F9.wireOp",EDGE,"E12.top"),sQuery(id+"F9.wireOp",EDGE,"E12.left"),sQuery(id+"F9.wireOp",EDGE,"E12.right")])],"isStart":false}),makeQuery(id+"F12.opExtrude","SWEPT_FACE",FACE,{"disambiguationData":[OSD([sQuery(id+"F11.wireOp",EDGE,"E17.10.0.2")])]})]});
            chamfer(context, id + "F17", {"entities" : qUnion([Q0, Q1, Q2, Q3, Q4, Q5, Q6, Q7, Q8, Q9, Q10, Q11, Q12, Q13, Q14, Q15, Q16, Q17]), "width" : .5 * mm, "tangentPropagation" : true});
        }
        {
            var Q0;
            Q0=makeQuery(id+"F7.opExtrude","SWEPT_FACE",FACE,{"disambiguationData":[OSD([sQuery(id+"F6.wireOp",EDGE,"E10.top")])]});
            cPlane(context, id + "F18", {"entities" : qUnion([Q0]), "cplaneType" : CPlaneType.OFFSET, "offset" : 1 * mm, "width" : 150 * mm, "height" : 150 * mm});
        }
        {
            var Q0;
            Q0=makeQuery(id+"F3.boolean.opBoolean","SPLIT",BODY,{"disambiguationData":[OD(0.0)],"derivedFrom":makeQuery(id+"F1.opExtrude","SWEPT_BODY",BODY,{"disambiguationData":[OSD([sQuery(id+"F0.wireOp",EDGE,"E0.bottom"),sQuery(id+"F0.wireOp",EDGE,"E0.top"),sQuery(id+"F0.wireOp",EDGE,"E0.left"),sQuery(id+"F0.wireOp",EDGE,"E0.right")])]})});
            var Q1;
            Q1=qCreatedBy(id+"F18.planeOp",FACE);
            mirror(context, id + "F19", {"entities" : qUnion([Q0]), "mirrorPlane" : qUnion([Q1])});
        }
        {
            var Q0;
            Q0=makeQuery(id+"F12.boolean.opBoolean","SPLIT",BODY,{"disambiguationData":[OD(0.0)],"derivedFrom":makeQuery(id+"F10.opExtrude","SWEPT_BODY",BODY,{"disambiguationData":[OSD([sQuery(id+"F9.wireOp",EDGE,"E12.bottom"),sQuery(id+"F9.wireOp",EDGE,"E12.top"),sQuery(id+"F9.wireOp",EDGE,"E12.left"),sQuery(id+"F9.wireOp",EDGE,"E12.right")])]})});
            var Q1;
            Q1=qCreatedBy(id+"F18.planeOp",FACE);
            mirror(context, id + "F20", {"entities" : qUnion([Q0]), "mirrorPlane" : qUnion([Q1])});
        }
    });
